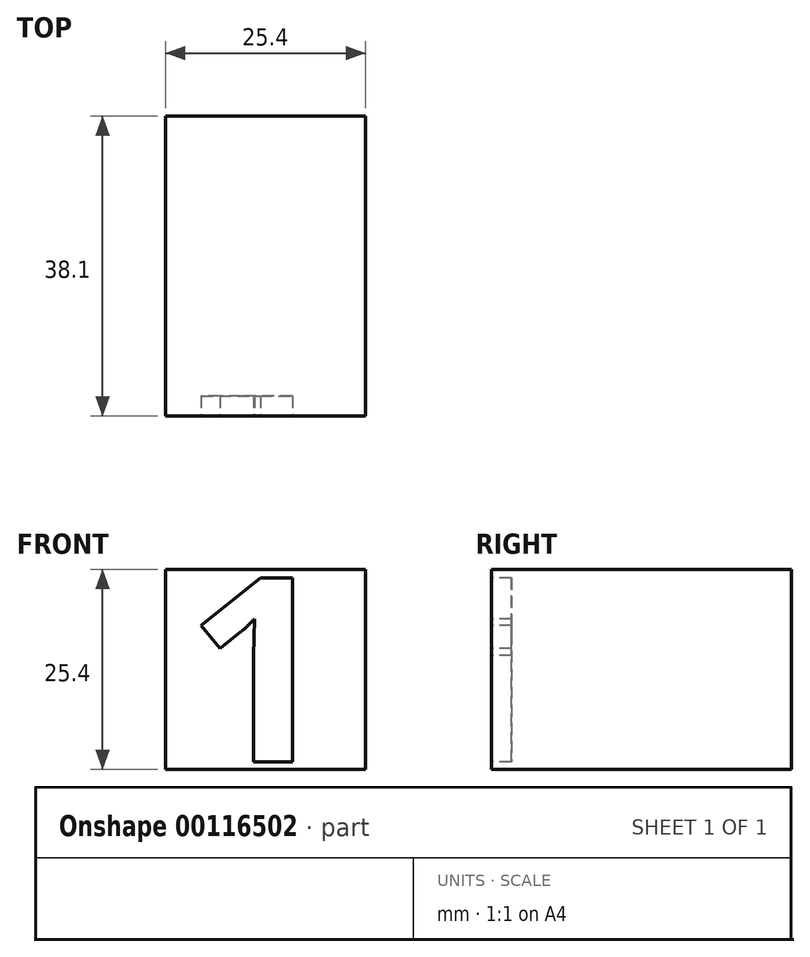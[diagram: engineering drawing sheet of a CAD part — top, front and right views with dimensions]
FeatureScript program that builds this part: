
annotation { "Feature Type Name" : "Feature", "Feature Type Description" : "" }
export const myFeature = defineFeature(function(context is Context, id is Id, definition is map)
    precondition{}
    {
        {
            var Q0;
            Q0=qCreatedBy(makeId("Front.planeOp"),FACE);
            var sketch = newSketch(context, id + "F0", { "sketchPlane" : qUnion([Q0])});
            skLineSegment(sketch, "E0.bottom", {"start": v(0, 0) * mm, "end": v(25.4, 0) * mm});
            skLineSegment(sketch, "E0.top", {"start": v(0, 25.4) * mm, "end": v(25.4, 25.4) * mm});
            skLineSegment(sketch, "E0.left", {"start": v(0, 0) * mm, "end": v(0, 25.4) * mm});
            skLineSegment(sketch, "E0.right", {"start": v(25.4, 0) * mm, "end": v(25.4, 25.4) * mm});
            skSolve(sketch);
        }
        {
            var Q0;
            Q0=makeQuery(id+"F0.imprint","IMPRINT",FACE,{"disambiguationData":[TD([[makeQuery(id+"F0.imprint","IMPRINT",EDGE,{"derivedFrom":sQuery(id+"F0.wireOp",EDGE,"E0.bottom")}),1.0]])]});
            extrude(context, id + "F1", {"entities" : qUnion([Q0]), "depth" : 38.1 * mm});
        }
        {
            var Q0;
            Q0=makeQuery(id+"F1.opExtrude","CAP_FACE",FACE,{"disambiguationData":[OSD([sQuery(id+"F0.wireOp",EDGE,"E0.bottom"),sQuery(id+"F0.wireOp",EDGE,"E0.top"),sQuery(id+"F0.wireOp",EDGE,"E0.left"),sQuery(id+"F0.wireOp",EDGE,"E0.right")])],"isStart":false});
            var sketch = newSketch(context, id + "F2", { "sketchPlane" : qUnion([Q0])});
            skText(sketch, "E1", { "text": "1", "fontName": "OpenSans-Bold.ttf"});
            const initialGuessF2  = {"E1": [0.0026, 0.00096, 1, 0, 0.02354]};
            skSetInitialGuess(sketch, initialGuessF2);
            skSolve(sketch);
        }
        {
            var Q0;
            Q0=makeQuery(id+"F2.imprint","IMPRINT",FACE,{"disambiguationData":[TD([[makeQuery(id+"F2.imprint","IMPRINT",EDGE,{"derivedFrom":sQuery(id+"F2.wireOp",EDGE,"E1.sketch_text.stroke-0")}),-1.0]])]});
            extrude(context, id + "F3", {"entities" : qUnion([Q0]), "operationType" : NewBodyOperationType.REMOVE, "oppositeDirection" : true, "depth" : 2.54 * mm});
        }
    });
